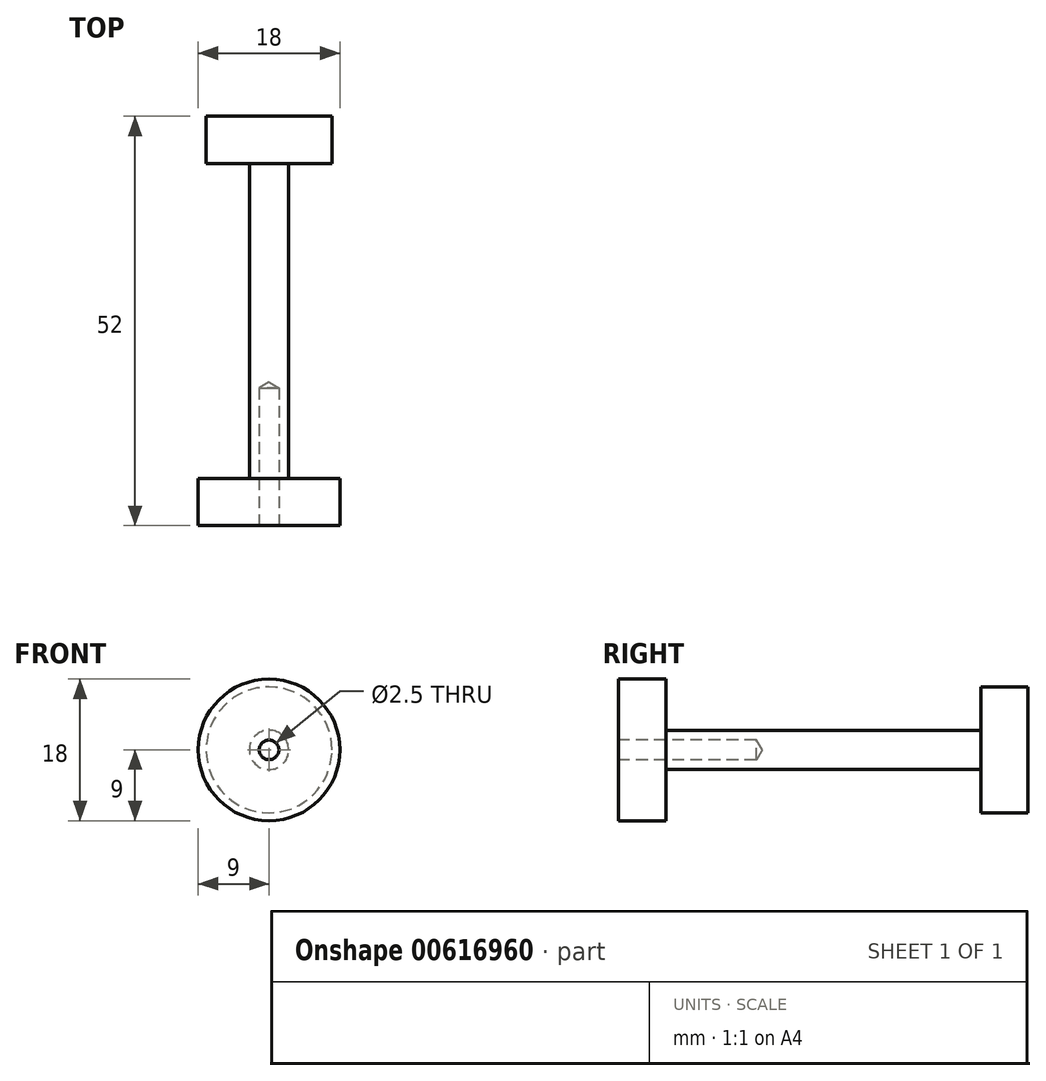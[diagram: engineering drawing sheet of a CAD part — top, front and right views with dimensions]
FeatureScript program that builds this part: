
annotation { "Feature Type Name" : "Feature", "Feature Type Description" : "" }
export const myFeature = defineFeature(function(context is Context, id is Id, definition is map)
    precondition{}
    {
        {
            var Q0;
            Q0=qCreatedBy(makeId("Front.planeOp"),FACE);
            var sketch = newSketch(context, id + "F0", { "sketchPlane" : qUnion([Q0])});
            skCircle(sketch, "E0", {"center": v(0, 0) * mm, "radius": 9 * mm});
            skSolve(sketch);
        }
        {
            var Q0;
            Q0=makeQuery(id+"F0.imprint","IMPRINT",FACE,{"disambiguationData":[TD([[makeQuery(id+"F0.imprint","IMPRINT",EDGE,{"derivedFrom":sQuery(id+"F0.wireOp",EDGE,"E0")}),1.0]])]});
            var Q1;
            Q1=sQuery(id+"F0.wireOp",EDGE,"E0");
            extrude(context, id + "F1", {"entities" : qUnion([Q0]), "surfaceEntities" : qUnion([Q1]), "depth" : 6 * mm, "offsetDistance" : 25 * mm});
        }
        {
            var Q0;
            Q0=qCreatedBy(makeId("Front.planeOp"),FACE);
            var sketch = newSketch(context, id + "F2", { "sketchPlane" : qUnion([Q0])});
            skCircle(sketch, "E1", {"center": v(0, 0) * mm, "radius": 2.5 * mm});
            skSolve(sketch);
        }
        {
            var Q0;
            Q0 = qSketchRegion(id + "F2", true);
            extrude(context, id + "F3", {"entities" : qUnion([Q0]), "operationType" : NewBodyOperationType.ADD, "oppositeDirection" : true, "depth" : 46 * mm, "offsetDistance" : 25 * mm});
        }
        {
            var Q0;
            Q0=makeQuery(id+"F3.opExtrude","CAP_FACE",FACE,{"disambiguationData":[OSD([sQuery(id+"F2.wireOp",EDGE,"E1")])],"isStart":false});
            var sketch = newSketch(context, id + "F4", { "sketchPlane" : qUnion([Q0])});
            skCircle(sketch, "E2", {"center": v(0, 0) * mm, "radius": 8 * mm});
            skSolve(sketch);
        }
        {
            var Q0;
            Q0=makeQuery(id+"F4.imprint","IMPRINT",FACE,{"disambiguationData":[TD([[makeQuery(id+"F4.imprint","IMPRINT",EDGE,{"derivedFrom":sQuery(id+"F4.wireOp",EDGE,"E2")}),1.0]])]});
            var Q1;
            Q1=sQuery(id+"F4.wireOp",EDGE,"E2");
            extrude(context, id + "F5", {"entities" : qUnion([Q0]), "operationType" : NewBodyOperationType.ADD, "surfaceEntities" : qUnion([Q1]), "oppositeDirection" : true, "depth" : 6 * mm, "offsetDistance" : 25 * mm});
        }
        {
            var Q0;
            Q0=makeQuery(id+"F1.opExtrude","CAP_FACE",FACE,{"disambiguationData":[OSD([sQuery(id+"F0.wireOp",EDGE,"E0")])],"isStart":false});
            var sketch = newSketch(context, id + "F6", { "sketchPlane" : qUnion([Q0])});
            skPoint(sketch, "E3", {"position": v(0, 0) * mm});
            skSolve(sketch);
        }
        {
            var Q0;
            Q0=sQuery(id+"F6.wireOp",VERTEX,"E3");
            var Q1;
            Q1=makeQuery(id+"F1.opExtrude","SWEPT_BODY",BODY,{"disambiguationData":[OSD([sQuery(id+"F0.wireOp",EDGE,"E0")])]});
            hole(context, id + "F7", {"style" : HoleStyle.SIMPLE, "endStyle" : HoleEndStyle.BLIND, "standardTappedOrClearance" : lookupTablePath({ "standard" : "ISO", "engagement" : "75%", "pitch" : "0.5 mm", "size" : "M3", "type" : "Tapped" }), "standardBlindInLast" : lookupTablePath({ "standard" : "ISO", "engagement" : "75%", "pitch" : "0.5 mm", "size" : "M3", "type" : "Tapped" }), "holeDiameter" : 2.5 * mm, "majorDiameter" : 3 * mm, "showTappedDepth" : true, "holeDepth" : 17.5 * mm, "isTappedThrough" : true, "tappedDepth" : 16 * mm, "tapClearance" : 3, "locations" : qUnion([Q0]), "scope" : qUnion([Q1])});
        }
    });
